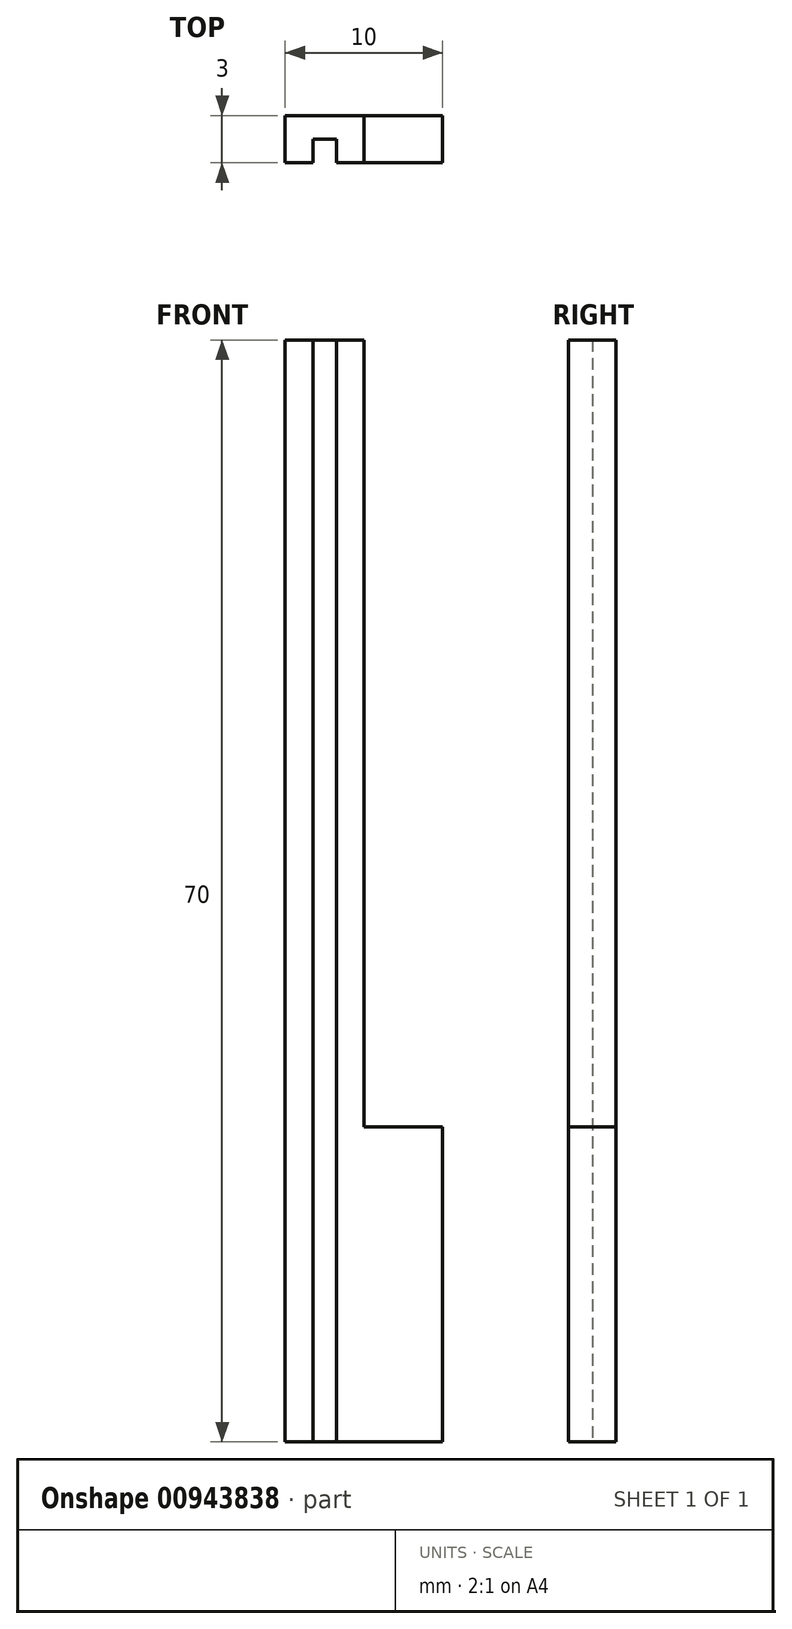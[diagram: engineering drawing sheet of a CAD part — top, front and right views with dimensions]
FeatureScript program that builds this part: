
annotation { "Feature Type Name" : "Feature", "Feature Type Description" : "" }
export const myFeature = defineFeature(function(context is Context, id is Id, definition is map)
    precondition{}
    {
        {
            var Q0;
            Q0=qCreatedBy(makeId("Front.planeOp"),FACE);
            var sketch = newSketch(context, id + "F0", { "sketchPlane" : qUnion([Q0])});
            skLineSegment(sketch, "E0.bottom", {"start": v(5, 0) * mm, "end": v(10, 0) * mm});
            skLineSegment(sketch, "E0.top", {"start": v(0, -20) * mm, "end": v(10, -20) * mm});
            skLineSegment(sketch, "E0.left", {"start": v(0, 0) * mm, "end": v(0, -20) * mm});
            skLineSegment(sketch, "E0.right", {"start": v(10, 0) * mm, "end": v(10, -20) * mm});
            skLineSegment(sketch, "E1.top", {"start": v(0, 50) * mm, "end": v(5, 50) * mm});
            skLineSegment(sketch, "E1.left", {"start": v(0, 0) * mm, "end": v(0, 50) * mm});
            skLineSegment(sketch, "E1.right", {"start": v(5, 0) * mm, "end": v(5, 50) * mm});
            skSolve(sketch);
        }
        {
            var Q0;
            Q0 = qSketchRegion(id + "F0", true);
            extrude(context, id + "F1", {"entities" : qUnion([Q0]), "depth" : 3 * mm, "offsetDistance" : 25 * mm});
        }
        {
            var Q0;
            Q0=makeQuery(id+"F1.opExtrude","CAP_FACE",FACE,{"disambiguationData":[OSD([sQuery(id+"F0.wireOp",EDGE,"E0.bottom"),sQuery(id+"F0.wireOp",EDGE,"E0.top"),sQuery(id+"F0.wireOp",EDGE,"E0.left"),sQuery(id+"F0.wireOp",EDGE,"E0.right"),sQuery(id+"F0.wireOp",EDGE,"E1.top"),sQuery(id+"F0.wireOp",EDGE,"E1.left"),sQuery(id+"F0.wireOp",EDGE,"E1.right")])],"isStart":false});
            var sketch = newSketch(context, id + "F2", { "sketchPlane" : qUnion([Q0])});
            skLineSegment(sketch, "E2.bottom", {"start": v(3.25, 50) * mm, "end": v(1.75, 50) * mm});
            skLineSegment(sketch, "E2.top", {"start": v(3.25, -20) * mm, "end": v(1.75, -20) * mm});
            skLineSegment(sketch, "E2.left", {"start": v(3.25, 50) * mm, "end": v(3.25, -20) * mm});
            skLineSegment(sketch, "E2.right", {"start": v(1.75, 50) * mm, "end": v(1.75, -20) * mm});
            skPoint(sketch, "E2.middle", {"position": v(2.5, 15) * mm});
            skPoint(sketch, "E2.middle.positionSnap0", {"position": v(2.5, 50) * mm});
            skPoint(sketch, "E2.centerSnap0", {"position": v(2.5, 50) * mm});
            skSolve(sketch);
        }
        {
            var Q0;
            Q0 = qSketchRegion(id + "F2", true);
            extrude(context, id + "F3", {"entities" : qUnion([Q0]), "operationType" : NewBodyOperationType.REMOVE, "oppositeDirection" : true, "depth" : 1.5 * mm, "offsetDistance" : 25 * mm});
        }
    });
